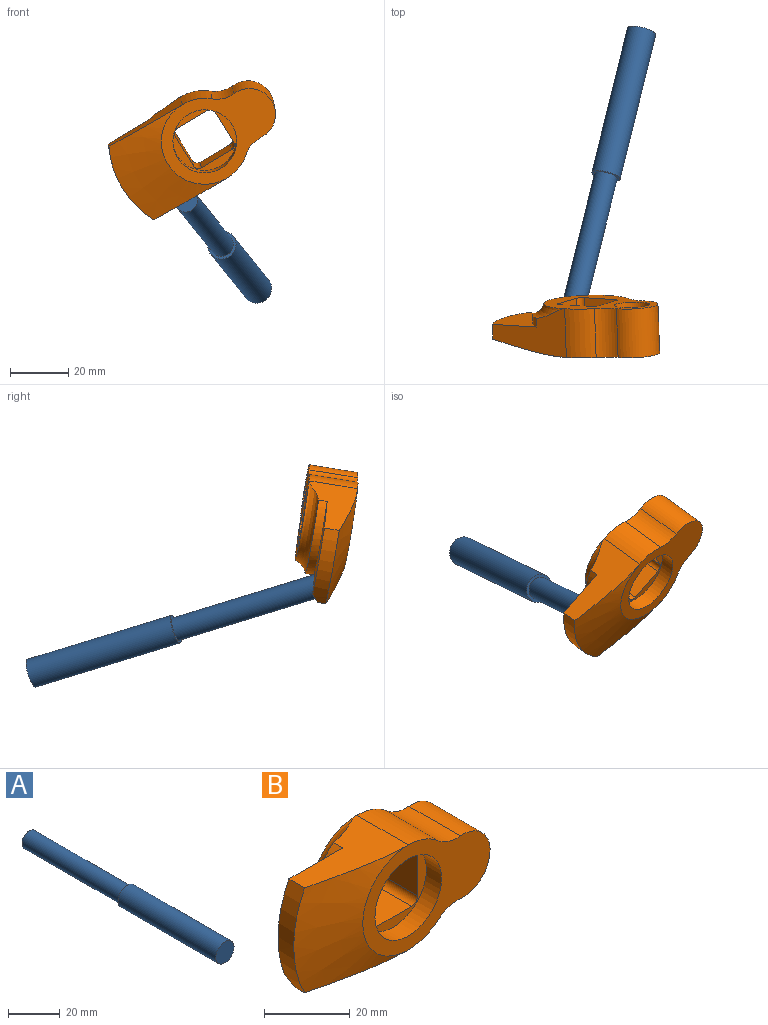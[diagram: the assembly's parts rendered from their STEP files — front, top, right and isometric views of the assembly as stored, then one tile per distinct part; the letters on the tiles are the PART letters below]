
ASSEMBLY  parts=2 mates=1
PART A: 5 faces, bbox 10x107.1x10 mm
  f0: cylinder r=4mm len=53.57mm, axis (0,1,0), area 1346.3mm2, adj f1,f4
  f1: plane 8x8mm, normal (0,1,0), area 50.3mm2, adj f0
  f2: cylinder r=5mm len=53.49mm, axis (0,1,0), area 1680.3mm2, adj f3,f4
  f3: plane 10x10mm, normal (0,-1,0), area 78.5mm2, adj f2
  f4: plane 10x10mm, normal (0,1,0), area 28.3mm2, adj f0,f2
PART B: 27 faces, bbox 60.2x18.1x66.2 mm
  f0: plane 42x30mm, normal (0,1,0), area 534.4mm2, adj f3,f6,f7,f8,f9,f10,f11,f12
  f1: plane 42x30mm, normal (0,-1,0), area 528.5mm2, adj f3,f6,f7,f8,f9,f18,f25
  f2: cylinder r=33mm len=30mm, axis (0,1,0), area 156.2mm2, adj f4,f5,f18,f23,f26
  f3: cylinder r=15mm len=17mm, axis (0,-1,0), area 181.6mm2, adj f0,f1,f4,f9
  f4: plane 29.4x17.01mm, normal (0,0,1), area 295.6mm2, adj f2,f3,f18,f21,f22,f23
  f5: plane 29.4x17.01mm, normal (0,0,-1), area 254.7mm2, adj f2,f6,f18,f21,f22,f26
  f6: cylinder r=15mm len=17mm, axis (0,-1,0), area 181.6mm2, adj f0,f1,f5,f7
  f7: cylinder r=10mm len=17mm, axis (0,-1,0), area 136mm2, adj f0,f1,f6,f8
  f8: cylinder r=9mm len=18mm, axis (0,-1,0), area 507.5mm2, adj f0,f1,f7,f9
  f9: cylinder r=10mm len=17mm, axis (0,-1,0), area 136mm2, adj f0,f1,f3,f8
  f10: plane 12.15x12mm, normal (0,0,1), area 145.8mm2, adj f0,f11,f17,f24
  f11: cylinder r=2mm len=12mm, axis (0,-1,0), area 37.7mm2, adj f0,f10,f12,f24
  f12: plane 12.15x12mm, normal (-1,0,0), area 145.8mm2, adj f0,f11,f13,f24
  f13: cylinder r=2mm len=12mm, axis (0,-1,0), area 37.7mm2, adj f0,f12,f14,f24
  f14: plane 12.15x12mm, normal (0,0,-1), area 145.8mm2, adj f0,f13,f15,f24
  f15: cylinder r=2mm len=12mm, axis (0,-1,0), area 37.7mm2, adj f0,f14,f16,f24
  f16: plane 12.15x12mm, normal (1,0,0), area 145.8mm2, adj f0,f15,f17,f24
  f17: cylinder r=2mm len=12mm, axis (0,-1,0), area 37.7mm2, adj f0,f10,f16,f24
  f18: cone r=15mm half-angle=75deg, axis (0,1,0), area 622.5mm2, adj f1,f2,f4,f5
  f19: cylinder r=6.1mm len=14.5mm, axis (0,1,0), area 555.7mm2, adj f0,f20
  f20: plane 12.2x12.2mm, normal (0,1,0), area 116.9mm2, adj f19
  f21: cylinder r=19mm len=30mm, axis (0,1,0), area 110.2mm2, adj f4,f5,f22,f23,f26
  f22: torus R=19.92mm, axis (0,1,0), area 232.2mm2, adj f0,f4,f5,f21
  f23: plane 26x21.34mm, normal (0,1,0), area 385.2mm2, adj f2,f4,f21,f26
  f24: plane 22x22mm, normal (0,-1,0), area 122.7mm2, adj f10,f11,f12,f13,f14,f15,f16,f17
  f25: cylinder r=11mm len=22mm, axis (0,1,0), area 345.6mm2, adj f1,f24
  f26: plane 19.61x4.16mm, normal (0,0.87,-0.5), area 76.4mm2, adj f2,f5,f21,f23
PLACE A rot(axis=(0.86,-0.17,-0.49),172.2deg) t=(296.83,3.8,-63.62)mm
PLACE B rot(axis=(0.29,-0.96,-0.02),32.6deg) t=(302.64,10.08,-40.38)mm
MATE planar A.f0 <-> B.f26  axis (-0.23,-0.93,0.28) through (296.83,3.8,-63.62)mm
